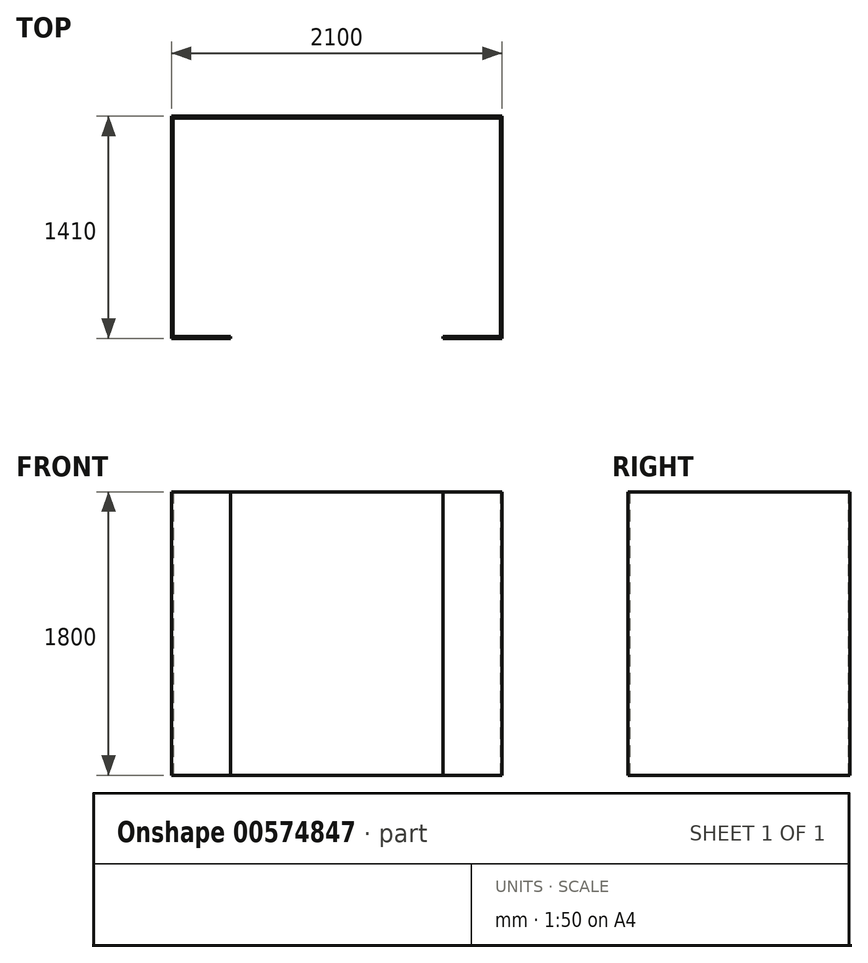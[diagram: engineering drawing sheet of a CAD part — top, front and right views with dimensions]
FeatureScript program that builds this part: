
annotation { "Feature Type Name" : "Feature", "Feature Type Description" : "" }
export const myFeature = defineFeature(function(context is Context, id is Id, definition is map)
    precondition{}
    {
        {
            var Q0;
            Q0=qCreatedBy(makeId("Top.planeOp"),FACE);
            var sketch = newSketch(context, id + "F0", { "sketchPlane" : qUnion([Q0])});
            skLineSegment(sketch, "E0.bottom", {"start": v(-1050, -705) * mm, "end": v(-675, -705) * mm});
            skLineSegment(sketch, "E0.top", {"start": v(-1050, 705) * mm, "end": v(1050, 705) * mm});
            skLineSegment(sketch, "E0.left", {"start": v(-1050, -705) * mm, "end": v(-1050, 705) * mm});
            skLineSegment(sketch, "E0.right", {"start": v(1050, -705) * mm, "end": v(1050, 705) * mm});
            skPoint(sketch, "E0.middle", {"position": v(0, 0) * mm});
            skLineSegment(sketch, "E1.bottom", {"start": v(-1040, -695) * mm, "end": v(-675, -695) * mm});
            skLineSegment(sketch, "E1.top", {"start": v(-1040, 695) * mm, "end": v(1040, 695) * mm});
            skLineSegment(sketch, "E1.left", {"start": v(-1040, -695) * mm, "end": v(-1040, 695) * mm});
            skLineSegment(sketch, "E1.right", {"start": v(1040, -695) * mm, "end": v(1040, 695) * mm});
            skLineSegment(sketch, "E2", {"start": v(-675, -705) * mm, "end": v(-675, -695) * mm});
            skLineSegment(sketch, "E3", {"start": v(675, -705) * mm, "end": v(675, -695) * mm});
            skLineSegment(sketch, "E4.trimOffspring", {"start": v(675, -705) * mm, "end": v(1050, -705) * mm});
            skLineSegment(sketch, "E5.trimOffspring", {"start": v(675, -695) * mm, "end": v(1040, -695) * mm});
            skSolve(sketch);
        }
        {
            var Q0;
            Q0 = qSketchRegion(id + "F0", true);
            extrude(context, id + "F1", {"entities" : qUnion([Q0]), "depth" : 1800 * mm, "offsetDistance" : 25 * mm});
        }
    });
